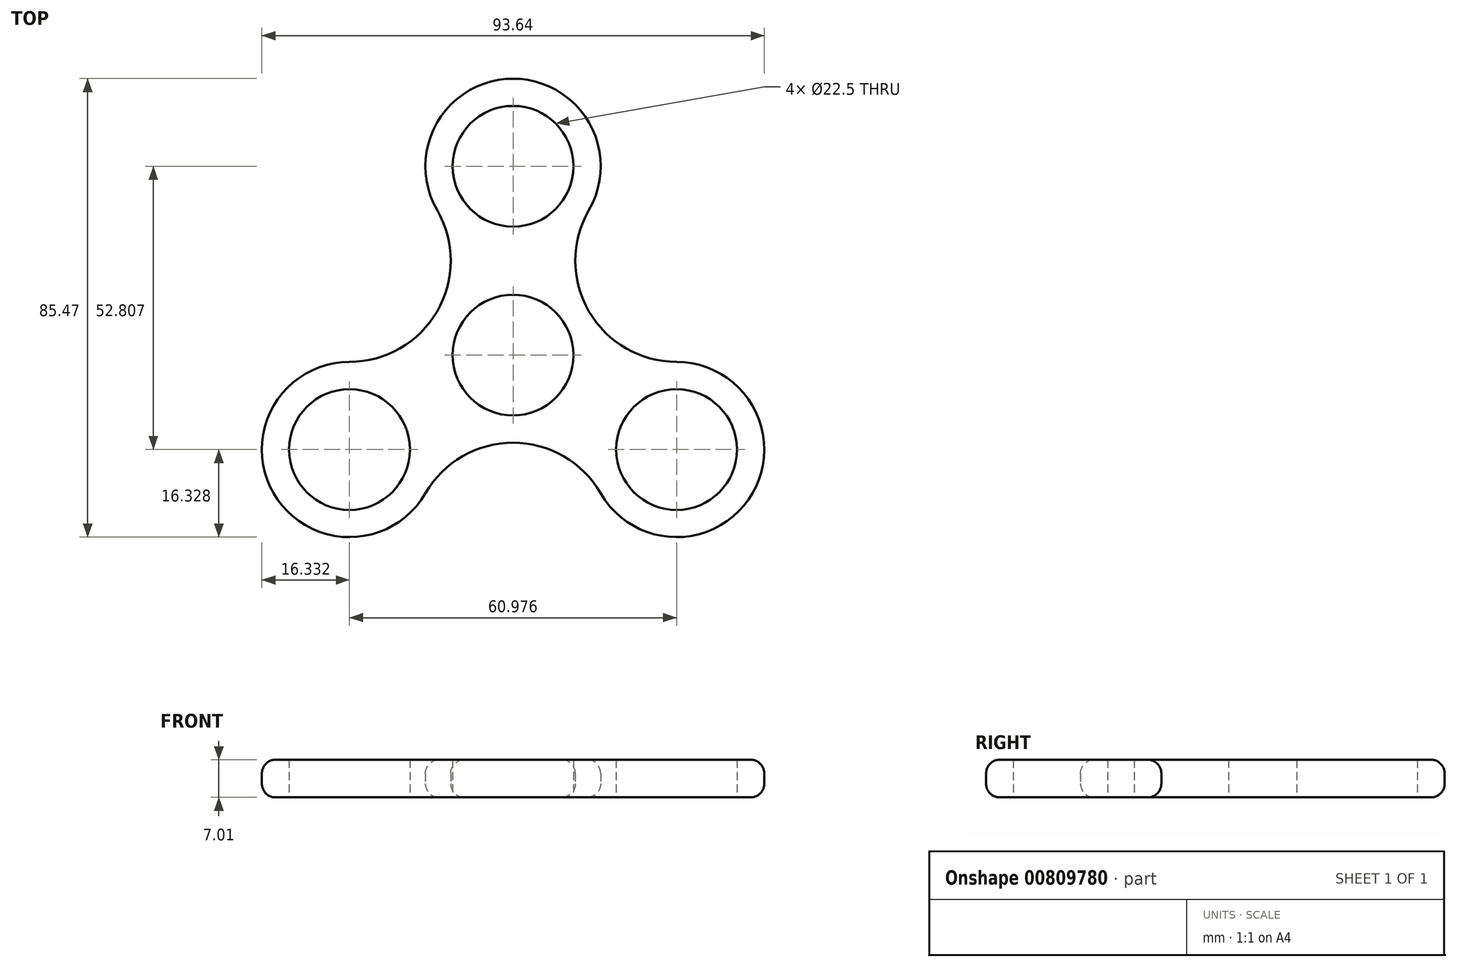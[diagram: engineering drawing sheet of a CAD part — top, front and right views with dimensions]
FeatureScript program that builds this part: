
annotation { "Feature Type Name" : "Feature", "Feature Type Description" : "" }
export const myFeature = defineFeature(function(context is Context, id is Id, definition is map)
    precondition{}
    {
        {
            var Q0;
            Q0=qCreatedBy(makeId("Top.planeOp"),FACE);
            var sketch = newSketch(context, id + "F0", { "sketchPlane" : qUnion([Q0])});
            skCircle(sketch, "E0", {"center": v(0, 0) * mm, "radius": 11.25 * mm});
            skCircle(sketch, "E1", {"center": v(0, 35.2) * mm, "radius": 11.25 * mm});
            skCircle(sketch, "E2", {"center": v(0, 35.2) * mm, "radius": 16.33 * mm});
            skCircle(sketch, "E3", {"center": v(0, 0) * mm, "radius": 16.33 * mm});
            skCircle(sketch, "E4.1.0", {"center": v(-30.49, -17.6) * mm, "radius": 11.25 * mm});
            skCircle(sketch, "E4.1.1", {"center": v(-30.49, -17.6) * mm, "radius": 16.33 * mm});
            skCircle(sketch, "E4.2.0", {"center": v(30.49, -17.6) * mm, "radius": 11.25 * mm});
            skCircle(sketch, "E4.2.1", {"center": v(30.49, -17.6) * mm, "radius": 16.33 * mm});
            skCircle(sketch, "E5", {"center": v(-30.49, 17.6) * mm, "radius": 18.87 * mm});
            skCircle(sketch, "E6.1.0", {"center": v(0, -35.2) * mm, "radius": 18.87 * mm});
            skCircle(sketch, "E6.2.0", {"center": v(30.49, 17.6) * mm, "radius": 18.87 * mm});
            skSolve(sketch);
        }
        {
            var Q0;
            Q0=makeQuery(id+"F0.imprint","IMPRINT",FACE,{"disambiguationData":[TD([[makeQuery(id+"F0.imprint","IMPRINT",EDGE,{"derivedFrom":sQuery(id+"F0.wireOp",EDGE,"E1")}),-1.0]])]});
            var Q1;
            Q1=makeQuery(id+"F0.imprint","IMPRINT",FACE,{"disambiguationData":[TD([[makeQuery(id+"F0.imprint","IMPRINT",EDGE,{"derivedFrom":sQuery(id+"F0.wireOp",EDGE,"E0")}),-1.0]])]});
            var Q2;
            Q2=makeQuery(id+"F0.imprint","IMPRINT",FACE,{"disambiguationData":[TD([[makeQuery(id+"F0.imprint","IMPRINT",EDGE,{"derivedFrom":sQuery(id+"F0.wireOp",EDGE,"E4.1.0")}),-1.0]])]});
            var Q3;
            {var subQ0=sQuery(id+"F0.wireOp",EDGE,"E5");var subQ1=sQuery(id+"F0.wireOp",EDGE,"E3");var subQ2=makeQuery(id+"F0.imprint","INTERSECT",VERTEX,{"derivedFrom":[subQ1,subQ0]});Q3=makeQuery(id+"F0.imprint","IMPRINT",FACE,{"disambiguationData":[TD([[makeQuery(id+"F0.imprint","IMPRINT",EDGE,{"disambiguationData":[TD([[subQ2,-1.0]])],"derivedFrom":subQ1}),-1.0]])]});}
            var Q4;
            {var subQ0=sQuery(id+"F0.wireOp",EDGE,"E5");var subQ1=sQuery(id+"F0.wireOp",EDGE,"E2");var subQ2=makeQuery(id+"F0.imprint","INTERSECT",VERTEX,{"derivedFrom":[subQ1,subQ0]});Q4=makeQuery(id+"F0.imprint","IMPRINT",FACE,{"disambiguationData":[TD([[makeQuery(id+"F0.imprint","IMPRINT",EDGE,{"disambiguationData":[TD([[subQ2,-1.0]])],"derivedFrom":subQ1}),-1.0]])]});}
            var Q5;
            {var subQ0=sQuery(id+"F0.wireOp",EDGE,"E6.2.0");var subQ1=sQuery(id+"F0.wireOp",EDGE,"E3");var subQ2=makeQuery(id+"F0.imprint","INTERSECT",VERTEX,{"derivedFrom":[subQ1,subQ0]});Q5=makeQuery(id+"F0.imprint","IMPRINT",FACE,{"disambiguationData":[TD([[makeQuery(id+"F0.imprint","IMPRINT",EDGE,{"disambiguationData":[TD([[subQ2,1.0]])],"derivedFrom":subQ1}),-1.0]])]});}
            var Q6;
            Q6=makeQuery(id+"F0.imprint","IMPRINT",FACE,{"disambiguationData":[TD([[makeQuery(id+"F0.imprint","IMPRINT",EDGE,{"derivedFrom":sQuery(id+"F0.wireOp",EDGE,"E4.2.0")}),-1.0]])]});
            extrude(context, id + "F1", {"entities" : qUnion([Q0, Q1, Q2, Q3, Q4, Q5, Q6]), "depth" : 7 * mm, "offsetDistance" : 25.4 * mm});
        }
        {
            var Q0;
            Q0=makeQuery(id+"F1.opExtrude","CAP_EDGE",EDGE,{"disambiguationData":[OSD([sQuery(id+"F0.wireOp",EDGE,"E2")])],"isStart":false});
            var Q1;
            Q1=makeQuery(id+"F1.opExtrude","CAP_EDGE",EDGE,{"disambiguationData":[OSD([sQuery(id+"F0.wireOp",EDGE,"E4.2.1")])],"isStart":true});
            var Q2;
            Q2=makeQuery(id+"F1.opExtrude","CAP_EDGE",EDGE,{"disambiguationData":[OSD([sQuery(id+"F0.wireOp",EDGE,"E6.2.0")])],"isStart":true});
            var Q3;
            Q3=makeQuery(id+"F1.opExtrude","CAP_EDGE",EDGE,{"disambiguationData":[OSD([sQuery(id+"F0.wireOp",EDGE,"E6.2.0")])],"isStart":false});
            fillet(context, id + "F2", {"entities" : qUnion([Q0, Q1, Q2, Q3]), "radius" : 2.54 * mm, "tangentPropagation" : true, "allowEdgeOverflow" : false});
        }
    });
